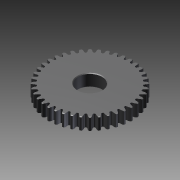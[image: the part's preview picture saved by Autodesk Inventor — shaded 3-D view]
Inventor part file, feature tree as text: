
AUTODESK INVENTOR PART (.ipt)
format: ipt  version: 2011 SP1 (Build 150282100, 282)  size: 1,188,864 bytes
history: native  units: mm
features: other x14, revolve x3, sketch x3, extrude x1, hole x1
ambient origin geometry x8: Origin, YZ Plane, XZ Plane, XY Plane, X Axis, Y Axis, Z Axis, Center Point
bodies: Solid1 (feature_tree)
feature tree (22):
  revolve  "Revolution1"  [1 undecoded]
  extrude  "Extrusion1"  TaperAngle=360.0deg  [1 undecoded]
  hole  "Hole1"  [1 undecoded]
  revolve  "Revolution2"  [1 undecoded]
  revolve  "Revolution3"  [1 undecoded]
  other  "b_XY"
  other  "b_YZ"
  other  "b_ZX"
  other  "b_X"
  other  "b_Y"
  other  "b_Z"
  other  "b_Center"
  other  "turn_around_XY"
  other  "turn_around_YZ"
  other  "turn_around_ZX"
  other  "turn_around_X"
  other  "turn_around_Y"
  other  "turn_around_Z"
  other  "turn_around_Center"
  sketch  "Sketch_12"  dims[d11=360.0deg d12=0.0mm]
  sketch  "Sketch_3"  dims[d0=360.0deg d1=6.0mm d2=0.0mm]
  sketch  "Sketch3"  dims[d3=12.0mm d4=6.0mm d5=4.0mm d6=2.0mm d7=90.0deg d8=6.0mm d9=0.0mm d10=360.0deg]
note: 5 required parameter values undecoded (feature->parameter linkage not recoverable at this tier; creation-order binding heuristic only, values carry confidence <= 0.55)